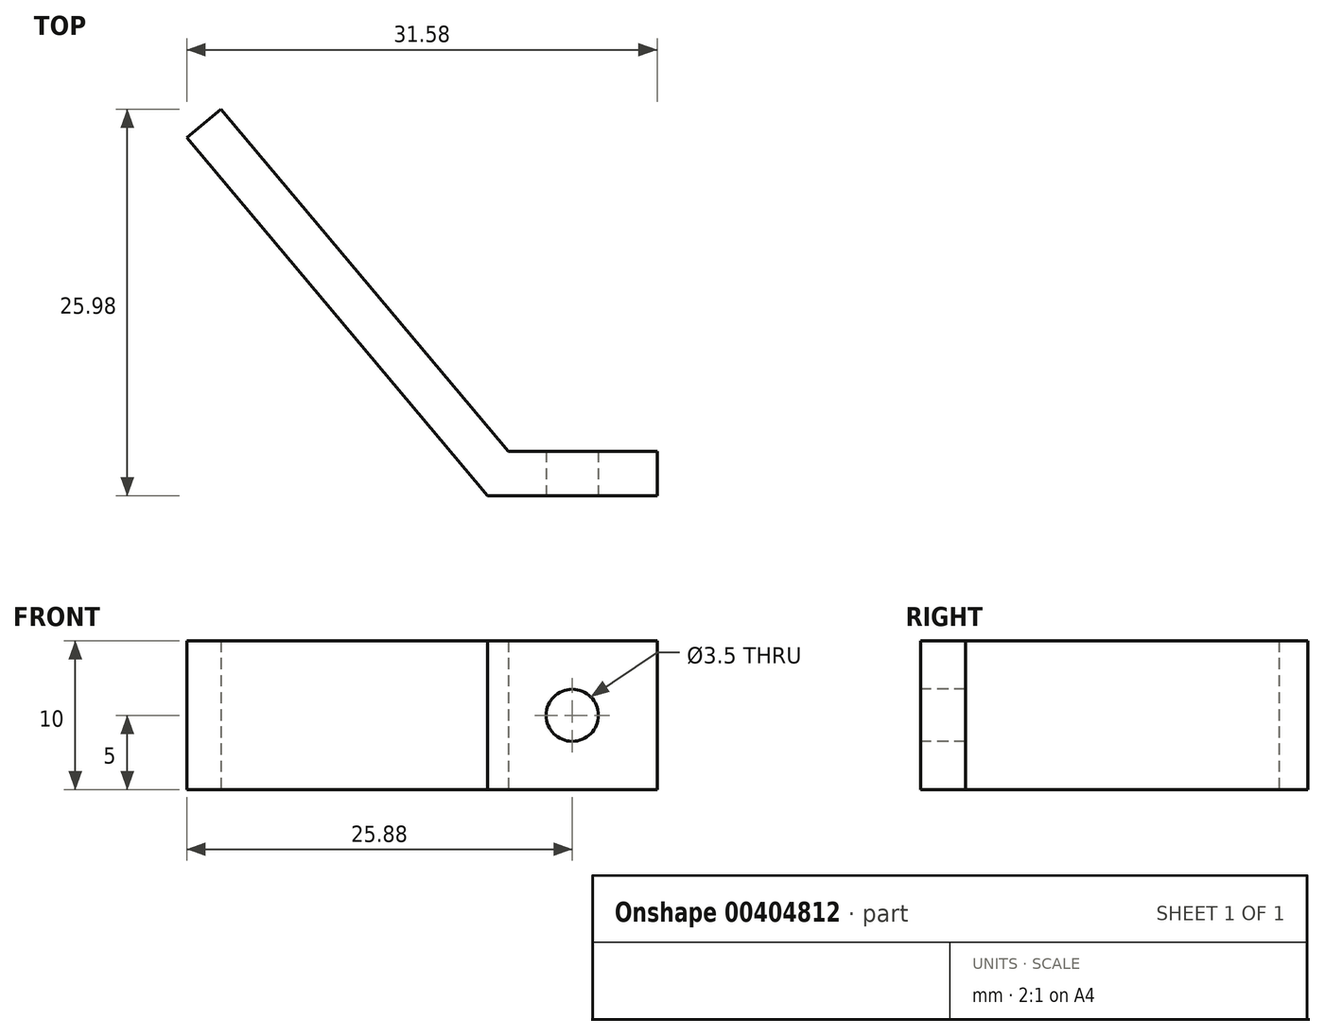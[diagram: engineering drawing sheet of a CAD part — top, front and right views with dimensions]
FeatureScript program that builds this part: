
annotation { "Feature Type Name" : "Feature", "Feature Type Description" : "" }
export const myFeature = defineFeature(function(context is Context, id is Id, definition is map)
    precondition{}
    {
        {
            var Q0;
            Q0=qCreatedBy(makeId("Top.planeOp"),FACE);
            var sketch = newSketch(context, id + "F0", { "sketchPlane" : qUnion([Q0])});
            skLineSegment(sketch, "E0", {"start": v(0, 0) * mm, "end": v(0, 3) * mm});
            skLineSegment(sketch, "E1", {"start": v(0, 3) * mm, "end": v(-10, 3) * mm});
            skLineSegment(sketch, "E2", {"start": v(-10, 3) * mm, "end": v(-29.28, 25.98) * mm});
            skLineSegment(sketch, "E3", {"start": v(-29.28, 25.98) * mm, "end": v(-31.58, 24.05) * mm});
            skLineSegment(sketch, "E4", {"start": v(-31.58, 24.05) * mm, "end": v(-11.4, 0) * mm});
            skLineSegment(sketch, "E5", {"start": v(-11.4, 0) * mm, "end": v(0, 0) * mm});
            skSolve(sketch);
        }
        {
            var Q0;
            Q0=makeQuery(id+"F0.imprint","IMPRINT",FACE,{"disambiguationData":[TD([[makeQuery(id+"F0.imprint","IMPRINT",EDGE,{"derivedFrom":sQuery(id+"F0.wireOp",EDGE,"E0")}),1.0]])]});
            extrude(context, id + "F1", {"entities" : qUnion([Q0]), "depth" : 10 * mm});
        }
        {
            var Q0;
            Q0=makeQuery(id+"F1.opExtrude","SWEPT_FACE",FACE,{"disambiguationData":[OSD([sQuery(id+"F0.wireOp",EDGE,"E5")])]});
            var sketch = newSketch(context, id + "F2", { "sketchPlane" : qUnion([Q0])});
            skLineSegment(sketch, "E6", {"start": v(-5.7, 10) * mm, "end": v(-5.7, 0) * mm, "construction": true});
            skLineSegment(sketch, "E7", {"start": v(0, 5) * mm, "end": v(-11.4, 5) * mm, "construction": true});
            skCircle(sketch, "E8", {"center": v(-5.7, 5) * mm, "radius": 1.75 * mm});
            skSolve(sketch);
        }
        {
            var Q0;
            Q0=makeQuery(id+"F2.imprint","IMPRINT",FACE,{"disambiguationData":[TD([[makeQuery(id+"F2.imprint","IMPRINT",EDGE,{"derivedFrom":sQuery(id+"F2.wireOp",EDGE,"E8")}),1.0]])]});
            extrude(context, id + "F3", {"entities" : qUnion([Q0]), "operationType" : NewBodyOperationType.REMOVE, "oppositeDirection" : true, "depth" : 3 * mm});
        }
    });
